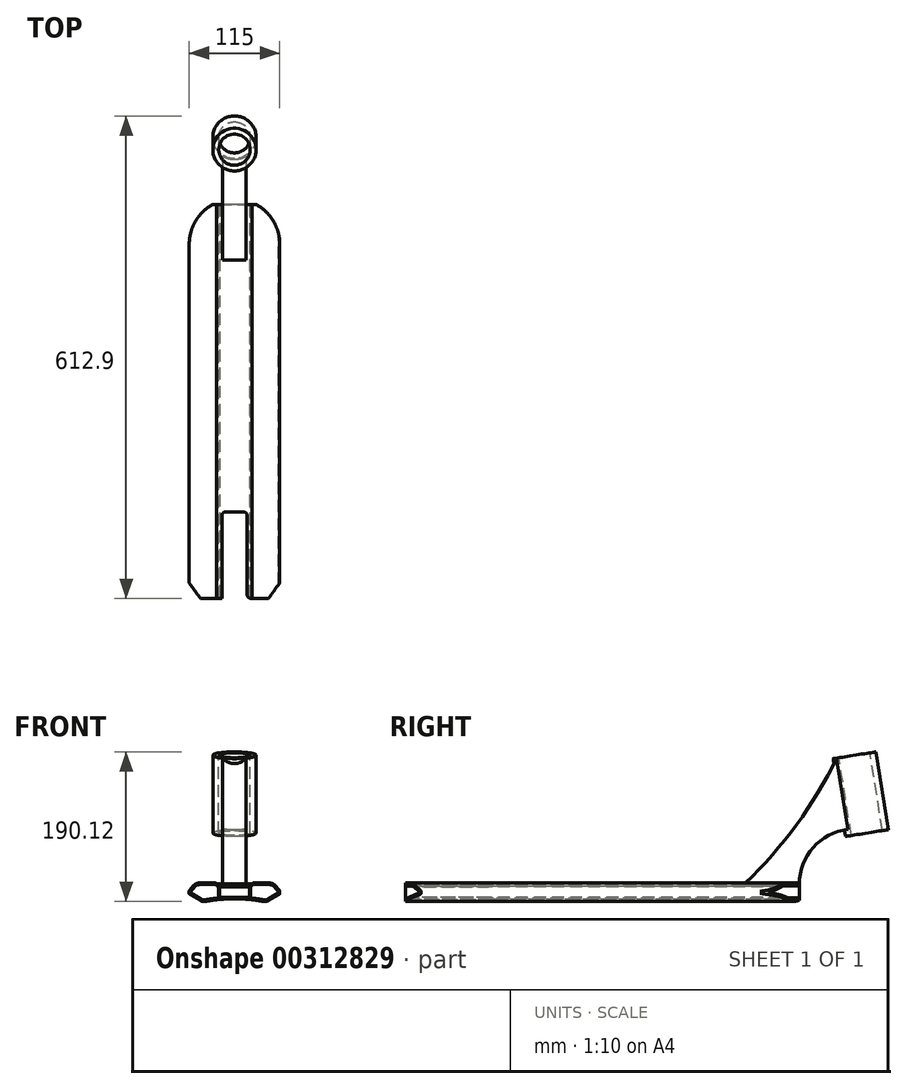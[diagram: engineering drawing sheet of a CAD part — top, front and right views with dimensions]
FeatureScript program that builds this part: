
annotation { "Feature Type Name" : "Feature", "Feature Type Description" : "" }
export const myFeature = defineFeature(function(context is Context, id is Id, definition is map)
    precondition{}
    {
        {
            var Q0;
            Q0=qCreatedBy(makeId("Front.planeOp"),FACE);
            var sketch = newSketch(context, id + "F0", { "sketchPlane" : qUnion([Q0])});
            skLineSegment(sketch, "E0", {"start": v(0, 0) * mm, "end": v(0, 20.54) * mm, "construction": true});
            skLineSegment(sketch, "E1", {"start": v(0, 0) * mm, "end": v(22.5, 0) * mm});
            skLineSegment(sketch, "E2", {"start": v(22.5, 0) * mm, "end": v(22.5, 1.3) * mm});
            skLineSegment(sketch, "E3", {"start": v(22.5, 1.3) * mm, "end": v(49.1, 1.3) * mm});
            skLineSegment(sketch, "E4", {"start": v(57.5, -8.7) * mm, "end": v(49.1, 1.3) * mm});
            skLineSegment(sketch, "E5", {"start": v(57.5, -8.7) * mm, "end": v(57.5, -12.7) * mm});
            skLineSegment(sketch, "E6", {"start": v(57.5, -12.7) * mm, "end": v(40.18, -22.7) * mm});
            skLineSegment(sketch, "E7.MirrorCS", {"start": v(0, 0) * mm, "end": v(-22.5, 0) * mm});
            skLineSegment(sketch, "E8.MirrorCS", {"start": v(-22.5, 0) * mm, "end": v(-22.5, 1.3) * mm});
            skLineSegment(sketch, "E9.MirrorCS", {"start": v(-22.5, 1.3) * mm, "end": v(-49.1, 1.3) * mm});
            skLineSegment(sketch, "E10.MirrorCS", {"start": v(-57.5, -8.7) * mm, "end": v(-49.1, 1.3) * mm});
            skLineSegment(sketch, "E11.MirrorCS", {"start": v(-57.5, -8.7) * mm, "end": v(-57.5, -12.7) * mm});
            skLineSegment(sketch, "E12.MirrorCS", {"start": v(-57.5, -12.7) * mm, "end": v(-40.18, -22.7) * mm});
            skArc(sketch, "E13", {"start": v(40.18, -22.7) * mm, "mid": v(0, -18.62) * mm, "end": v(-40.18, -22.7) * mm});
            skSolve(sketch);
        }
        {
            var Q0;
            Q0 = qSketchRegion(id + "F0", true);
            extrude(context, id + "F1", {"entities" : qUnion([Q0]), "endBound" : BoundingType.SYMMETRIC, "depth" : 500 * mm});
        }
        {
            var Q0;
            Q0=qCreatedBy(makeId("Front.planeOp"),FACE);
            var sketch = newSketch(context, id + "F2", { "sketchPlane" : qUnion([Q0])});
            skLineSegment(sketch, "E14.bottom", {"start": v(-19, -16.75) * mm, "end": v(19, -16.75) * mm});
            skLineSegment(sketch, "E14.top", {"start": v(-19, -3.75) * mm, "end": v(19, -3.75) * mm});
            skLineSegment(sketch, "E14.left", {"start": v(-19, -16.75) * mm, "end": v(-19, -3.75) * mm});
            skLineSegment(sketch, "E14.right", {"start": v(19, -16.75) * mm, "end": v(19, -3.75) * mm});
            skPoint(sketch, "E14.middle", {"position": v(0, -10.25) * mm});
            skSolve(sketch);
        }
        {
            var Q0;
            Q0 = qSketchRegion(id + "F2", true);
            extrude(context, id + "F3", {"entities" : qUnion([Q0]), "operationType" : NewBodyOperationType.REMOVE, "endBound" : BoundingType.SYMMETRIC, "oppositeDirection" : true, "depth" : 500 * mm});
        }
        {
            var Q0;
            Q0=makeQuery(id+"F1.opExtrude","SWEPT_EDGE",EDGE,{"disambiguationData":[OSD([sQuery(id+"F0.wireOp",EDGE,"E2"),sQuery(id+"F0.wireOp",EDGE,"E3")])]});
            var Q1;
            Q1=makeQuery(id+"F1.opExtrude","SWEPT_EDGE",EDGE,{"disambiguationData":[OSD([sQuery(id+"F0.wireOp",EDGE,"E8.MirrorCS"),sQuery(id+"F0.wireOp",EDGE,"E9.MirrorCS")])]});
            fillet(context, id + "F4", {"entities" : qUnion([Q0, Q1]), "radius" : 2 * mm, "tangentPropagation" : true, "allowEdgeOverflow" : false});
        }
        {
            var Q0;
            Q0=makeQuery(id+"F1.opExtrude","SWEPT_EDGE",EDGE,{"disambiguationData":[OSD([sQuery(id+"F0.wireOp",EDGE,"E9.MirrorCS"),sQuery(id+"F0.wireOp",EDGE,"E10.MirrorCS")])]});
            var Q1;
            Q1=makeQuery(id+"F1.opExtrude","SWEPT_EDGE",EDGE,{"disambiguationData":[OSD([sQuery(id+"F0.wireOp",EDGE,"E3"),sQuery(id+"F0.wireOp",EDGE,"E4")])]});
            var Q2;
            Q2=makeQuery(id+"F1.opExtrude","SWEPT_EDGE",EDGE,{"disambiguationData":[OSD([sQuery(id+"F0.wireOp",EDGE,"E6"),sQuery(id+"F0.wireOp",EDGE,"E13")])]});
            var Q3;
            Q3=makeQuery(id+"F1.opExtrude","SWEPT_EDGE",EDGE,{"disambiguationData":[OSD([sQuery(id+"F0.wireOp",EDGE,"E12.MirrorCS"),sQuery(id+"F0.wireOp",EDGE,"E13")])]});
            fillet(context, id + "F5", {"entities" : qUnion([Q0, Q1, Q2, Q3]), "radius" : 9 * mm, "tangentPropagation" : true, "allowEdgeOverflow" : false});
        }
        {
            var Q0;
            Q0=makeQuery(id+"F1.opExtrude","SWEPT_EDGE",EDGE,{"disambiguationData":[OSD([sQuery(id+"F0.wireOp",EDGE,"E10.MirrorCS"),sQuery(id+"F0.wireOp",EDGE,"E11.MirrorCS")])]});
            var Q1;
            Q1=makeQuery(id+"F1.opExtrude","SWEPT_EDGE",EDGE,{"disambiguationData":[OSD([sQuery(id+"F0.wireOp",EDGE,"E11.MirrorCS"),sQuery(id+"F0.wireOp",EDGE,"E12.MirrorCS")])]});
            var Q2;
            Q2=makeQuery(id+"F1.opExtrude","SWEPT_EDGE",EDGE,{"disambiguationData":[OSD([sQuery(id+"F0.wireOp",EDGE,"E4"),sQuery(id+"F0.wireOp",EDGE,"E5")])]});
            var Q3;
            Q3=makeQuery(id+"F1.opExtrude","SWEPT_EDGE",EDGE,{"disambiguationData":[OSD([sQuery(id+"F0.wireOp",EDGE,"E5"),sQuery(id+"F0.wireOp",EDGE,"E6")])]});
            fillet(context, id + "F6", {"entities" : qUnion([Q0, Q1, Q2, Q3]), "radius" : 2 * mm, "tangentPropagation" : true, "allowEdgeOverflow" : false});
        }
        {
            var Q0;
            Q0=makeQuery(id+"F1.opExtrude","CAP_FACE",FACE,{"disambiguationData":[OSD([sQuery(id+"F0.wireOp",EDGE,"E1"),sQuery(id+"F0.wireOp",EDGE,"E2"),sQuery(id+"F0.wireOp",EDGE,"E3"),sQuery(id+"F0.wireOp",EDGE,"E4"),sQuery(id+"F0.wireOp",EDGE,"E5"),sQuery(id+"F0.wireOp",EDGE,"E6"),sQuery(id+"F0.wireOp",EDGE,"E7.MirrorCS"),sQuery(id+"F0.wireOp",EDGE,"E8.MirrorCS"),sQuery(id+"F0.wireOp",EDGE,"E9.MirrorCS"),sQuery(id+"F0.wireOp",EDGE,"E10.MirrorCS"),sQuery(id+"F0.wireOp",EDGE,"E11.MirrorCS"),sQuery(id+"F0.wireOp",EDGE,"E12.MirrorCS"),sQuery(id+"F0.wireOp",EDGE,"E13")])],"isStart":false});
            var sketch = newSketch(context, id + "F7", { "sketchPlane" : qUnion([Q0])});
            skArc(sketch, "E15.0", {"start": v(-20.4, -17.65) * mm, "mid": v(-28.88, -18.7) * mm, "end": v(-37.3, -20.1) * mm});
            skArc(sketch, "E15.1", {"start": v(-42.1, -19.28) * mm, "mid": v(-39.78, -20.12) * mm, "end": v(-37.3, -20.1) * mm});
            skLineSegment(sketch, "E15.2", {"start": v(-24.37, -0.7) * mm, "end": v(-44.91, -0.7) * mm});
            skArc(sketch, "E15.3", {"start": v(-44.91, -0.7) * mm, "mid": v(-47.87, -1.36) * mm, "end": v(-50.27, -3.2) * mm});
            skLineSegment(sketch, "E15.4", {"start": v(-55.93, -9.94) * mm, "end": v(-50.27, -3.2) * mm});
            skLineSegment(sketch, "E15.5", {"start": v(-55.66, -11.45) * mm, "end": v(-42.1, -19.28) * mm});
            skPoint(sketch, "E16.visualSharp", {"position": v(-56.7, -10.85) * mm});
            skArc(sketch, "E16.filletArc", {"start": v(-55.93, -9.94) * mm, "mid": v(-56.15, -10.76) * mm, "end": v(-55.66, -11.45) * mm});
            skArc(sketch, "E17", {"start": v(-24.37, -0.7) * mm, "mid": v(-23.06, -1.19) * mm, "end": v(-22.4, -2.41) * mm});
            skLineSegment(sketch, "E18", {"start": v(-22.4, -2.41) * mm, "end": v(-20.4, -2.41) * mm});
            skLineSegment(sketch, "E19", {"start": v(-20.4, -2.41) * mm, "end": v(-20.4, -17.65) * mm});
            skLineSegment(sketch, "E20", {"start": v(0, 0) * mm, "end": v(0, 20.39) * mm, "construction": true});
            skPoint(sketch, "E20.endSnap0", {"position": v(0, 0) * mm});
            skLineSegment(sketch, "E21.MirrorCS", {"start": v(20.4, -2.41) * mm, "end": v(20.4, -17.65) * mm});
            skLineSegment(sketch, "E22.MirrorCS", {"start": v(22.4, -2.41) * mm, "end": v(20.4, -2.41) * mm});
            skArc(sketch, "E23.MirrorCS", {"start": v(24.37, -0.7) * mm, "mid": v(23.06, -1.19) * mm, "end": v(22.4, -2.41) * mm});
            skLineSegment(sketch, "E24.MirrorCS", {"start": v(24.37, -0.7) * mm, "end": v(44.91, -0.7) * mm});
            skArc(sketch, "E25.MirrorCS", {"start": v(44.91, -0.7) * mm, "mid": v(47.87, -1.36) * mm, "end": v(50.27, -3.2) * mm});
            skLineSegment(sketch, "E26.MirrorCS", {"start": v(55.93, -9.94) * mm, "end": v(50.27, -3.2) * mm});
            skLineSegment(sketch, "E27.MirrorCS", {"start": v(55.66, -11.45) * mm, "end": v(42.1, -19.28) * mm});
            skArc(sketch, "E28.MirrorCS", {"start": v(42.1, -19.28) * mm, "mid": v(39.78, -20.12) * mm, "end": v(37.3, -20.1) * mm});
            skArc(sketch, "E29.MirrorCS", {"start": v(20.4, -17.65) * mm, "mid": v(28.88, -18.7) * mm, "end": v(37.3, -20.1) * mm});
            skArc(sketch, "E30.MirrorCS", {"start": v(55.93, -9.94) * mm, "mid": v(56.15, -10.76) * mm, "end": v(55.66, -11.45) * mm});
            skSolve(sketch);
        }
        {
            var Q0;
            Q0 = qSketchRegion(id + "F7", true);
            extrude(context, id + "F8", {"entities" : qUnion([Q0]), "operationType" : NewBodyOperationType.REMOVE, "endBound" : BoundingType.THROUGH_ALL, "depth" : 25 * mm, "hasSecondDirection" : true, "secondDirectionBound" : SecondDirectionBoundingType.THROUGH_ALL, "secondDirectionOppositeDirection" : true, "secondDirectionDepth" : 25 * mm});
        }
        {
            var Q0;
            Q0=qCreatedBy(makeId("Top.planeOp"),FACE);
            var sketch = newSketch(context, id + "F9", { "sketchPlane" : qUnion([Q0])});
            skArc(sketch, "E31", {"start": v(57.5, 200) * mm, "mid": v(0, 257.5) * mm, "end": v(-57.5, 200) * mm});
            skLineSegment(sketch, "E32", {"start": v(-57.5, 200) * mm, "end": v(-57.5, 280) * mm});
            skLineSegment(sketch, "E33", {"start": v(-57.5, 280) * mm, "end": v(57.5, 280) * mm});
            skLineSegment(sketch, "E34", {"start": v(57.5, 280) * mm, "end": v(57.5, 200) * mm});
            skSolve(sketch);
        }
        {
            var Q0;
            Q0 = qSketchRegion(id + "F9", true);
            extrude(context, id + "F10", {"entities" : qUnion([Q0]), "operationType" : NewBodyOperationType.REMOVE, "endBound" : BoundingType.THROUGH_ALL, "oppositeDirection" : true, "depth" : 25 * mm, "hasSecondDirection" : true, "secondDirectionBound" : SecondDirectionBoundingType.THROUGH_ALL, "secondDirectionOppositeDirection" : false, "secondDirectionDepth" : 25 * mm});
        }
        {
            var Q0;
            Q0=qCreatedBy(makeId("Top.planeOp"),FACE);
            var sketch = newSketch(context, id + "F11", { "sketchPlane" : qUnion([Q0])});
            skLineSegment(sketch, "E35", {"start": v(-68, -216) * mm, "end": v(-43.3, -250) * mm});
            skLineSegment(sketch, "E36", {"start": v(-43.3, -250) * mm, "end": v(-16, -250) * mm});
            skLineSegment(sketch, "E37", {"start": v(-16, -250) * mm, "end": v(-16, -140) * mm});
            skLineSegment(sketch, "E38", {"start": v(-16, -140) * mm, "end": v(16, -140) * mm});
            skLineSegment(sketch, "E39", {"start": v(16, -140) * mm, "end": v(16, -250) * mm});
            skLineSegment(sketch, "E40", {"start": v(16, -250) * mm, "end": v(43.3, -250) * mm});
            skLineSegment(sketch, "E41", {"start": v(43.3, -250) * mm, "end": v(68, -216) * mm});
            skLineSegment(sketch, "E42", {"start": v(68, -216) * mm, "end": v(68, -346) * mm});
            skLineSegment(sketch, "E43", {"start": v(68, -346) * mm, "end": v(-68, -346) * mm});
            skLineSegment(sketch, "E44", {"start": v(-68, -346) * mm, "end": v(-68, -216) * mm});
            skSolve(sketch);
        }
        {
            var Q0;
            Q0 = qSketchRegion(id + "F11", true);
            extrude(context, id + "F12", {"entities" : qUnion([Q0]), "operationType" : NewBodyOperationType.REMOVE, "endBound" : BoundingType.THROUGH_ALL, "depth" : 25 * mm, "hasSecondDirection" : true, "secondDirectionBound" : SecondDirectionBoundingType.THROUGH_ALL, "secondDirectionOppositeDirection" : true, "secondDirectionDepth" : 25 * mm});
        }
        {
            var Q0;
            {var subQ2=sQuery(id+"F11.wireOp",EDGE,"E39");Q0=makeQuery(id+"F12.boolean.opBoolean","COPY",EDGE,{"disambiguationData":[TD([makeQuery(id+"F3.boolean.opBoolean","COPY",FACE,{"derivedFrom":makeQuery(id+"F3.opExtrude","SWEPT_FACE",FACE,{"disambiguationData":[OSD([sQuery(id+"F2.wireOp",EDGE,"E14.top")])]})})])],"derivedFrom":makeQuery(id+"F12.opExtrude","SWEPT_EDGE",EDGE,{"disambiguationData":[OSD([subQ2,sQuery(id+"F11.wireOp",EDGE,"E40")])]})});}
            var Q1;
            {var subQ2=sQuery(id+"F11.wireOp",EDGE,"E37");Q1=makeQuery(id+"F12.boolean.opBoolean","COPY",EDGE,{"disambiguationData":[TD([makeQuery(id+"F3.boolean.opBoolean","COPY",FACE,{"derivedFrom":makeQuery(id+"F3.opExtrude","SWEPT_FACE",FACE,{"disambiguationData":[OSD([sQuery(id+"F2.wireOp",EDGE,"E14.top")])]})})])],"derivedFrom":makeQuery(id+"F12.opExtrude","SWEPT_EDGE",EDGE,{"disambiguationData":[OSD([sQuery(id+"F11.wireOp",EDGE,"E36"),subQ2])]})});}
            var Q2;
            {var subQ0=sQuery(id+"F11.wireOp",EDGE,"E37");var subQ1=sQuery(id+"F11.wireOp",EDGE,"E38");Q2=makeQuery(id+"F12.boolean.opBoolean","COPY",EDGE,{"disambiguationData":[TD([makeQuery(id+"F3.boolean.opBoolean","COPY",FACE,{"derivedFrom":makeQuery(id+"F3.opExtrude","SWEPT_FACE",FACE,{"disambiguationData":[OSD([sQuery(id+"F2.wireOp",EDGE,"E14.top")])]})})])],"derivedFrom":makeQuery(id+"F12.opExtrude","SWEPT_EDGE",EDGE,{"disambiguationData":[OSD([subQ0,subQ1])]})});}
            var Q3;
            {var subQ0=sQuery(id+"F11.wireOp",EDGE,"E38");var subQ1=sQuery(id+"F11.wireOp",EDGE,"E37");Q3=makeQuery(id+"F12.boolean.opBoolean","COPY",EDGE,{"disambiguationData":[TD([makeQuery(id+"F1.opExtrude","SWEPT_FACE",FACE,{"disambiguationData":[OSD([sQuery(id+"F0.wireOp",EDGE,"E13")])]})])],"derivedFrom":makeQuery(id+"F12.opExtrude","SWEPT_EDGE",EDGE,{"disambiguationData":[OSD([subQ1,subQ0])]})});}
            var Q4;
            {var subQ0=sQuery(id+"F11.wireOp",EDGE,"E39");var subQ1=sQuery(id+"F11.wireOp",EDGE,"E38");Q4=makeQuery(id+"F12.boolean.opBoolean","COPY",EDGE,{"disambiguationData":[TD([makeQuery(id+"F3.boolean.opBoolean","COPY",FACE,{"derivedFrom":makeQuery(id+"F3.opExtrude","SWEPT_FACE",FACE,{"disambiguationData":[OSD([sQuery(id+"F2.wireOp",EDGE,"E14.top")])]})})])],"derivedFrom":makeQuery(id+"F12.opExtrude","SWEPT_EDGE",EDGE,{"disambiguationData":[OSD([subQ1,subQ0])]})});}
            var Q5;
            {var subQ0=sQuery(id+"F11.wireOp",EDGE,"E38");var subQ1=sQuery(id+"F11.wireOp",EDGE,"E39");Q5=makeQuery(id+"F12.boolean.opBoolean","COPY",EDGE,{"disambiguationData":[TD([makeQuery(id+"F1.opExtrude","SWEPT_FACE",FACE,{"disambiguationData":[OSD([sQuery(id+"F0.wireOp",EDGE,"E13")])]})])],"derivedFrom":makeQuery(id+"F12.opExtrude","SWEPT_EDGE",EDGE,{"disambiguationData":[OSD([subQ0,subQ1])]})});}
            fillet(context, id + "F13", {"entities" : qUnion([Q0, Q1, Q2, Q3, Q4, Q5]), "radius" : 5 * mm, "tangentPropagation" : true, "allowEdgeOverflow" : false});
        }
        {
            var Q0;
            Q0=qCreatedBy(makeId("Right.planeOp"),FACE);
            var sketch = newSketch(context, id + "F14", { "sketchPlane" : qUnion([Q0])});
            skLineSegment(sketch, "E45", {"start": v(180, 0) * mm, "end": v(250, 0) * mm});
            skArc(sketch, "E46", {"start": v(180, 0) * mm, "mid": v(245.97, 74.66) * mm, "end": v(297.38, 160) * mm});
            skLineSegment(sketch, "E47", {"start": v(297.38, 160) * mm, "end": v(342.82, 167.2) * mm});
            skLineSegment(sketch, "E48", {"start": v(342.82, 167.2) * mm, "end": v(358.46, 68.43) * mm});
            skLineSegment(sketch, "E49", {"start": v(358.46, 68.43) * mm, "end": v(313.03, 61.23) * mm});
            skLineSegment(sketch, "E50", {"start": v(313.03, 61.23) * mm, "end": v(311.71, 69.5) * mm});
            skArc(sketch, "E51", {"start": v(311.71, 69.5) * mm, "mid": v(267.66, 46.48) * mm, "end": v(250, 0) * mm});
            skSolve(sketch);
        }
        {
            var Q0;
            Q0 = qSketchRegion(id + "F14", true);
            extrude(context, id + "F15", {"entities" : qUnion([Q0]), "operationType" : NewBodyOperationType.ADD, "endBound" : BoundingType.SYMMETRIC, "depth" : 30 * mm});
        }
        {
            var Q0;
            Q0=makeQuery(id+"F15.opExtrude","SWEPT_FACE",FACE,{"disambiguationData":[OSD([sQuery(id+"F14.wireOp",EDGE,"E47")])]});
            var sketch = newSketch(context, id + "F16", { "sketchPlane" : qUnion([Q0])});
            skCircle(sketch, "E52", {"center": v(0, 341.75) * mm, "radius": 27.5 * mm});
            skSolve(sketch);
        }
        {
            var Q0;
            Q0 = qSketchRegion(id + "F16", true);
            var Q1;
            Q1=makeQuery(id+"F15.opExtrude","SWEPT_FACE",FACE,{"disambiguationData":[OSD([sQuery(id+"F14.wireOp",EDGE,"E49")])]});
            extrude(context, id + "F17", {"entities" : qUnion([Q0]), "operationType" : NewBodyOperationType.ADD, "endBound" : BoundingType.UP_TO_SURFACE, "oppositeDirection" : true, "endBoundEntityFace" : qUnion([Q1]), "depth" : 25 * mm});
        }
        {
            var Q0;
            Q0=makeQuery(id+"F17.boolean.opBoolean","MERGE",FACE,{"derivedFrom":[makeQuery(id+"F15.opExtrude","SWEPT_FACE",FACE,{"disambiguationData":[OSD([sQuery(id+"F14.wireOp",EDGE,"E47")])]}),makeQuery(id+"F17.opExtrude","CAP_FACE",FACE,{"disambiguationData":[OSD([sQuery(id+"F16.wireOp",EDGE,"E52")])],"isStart":true})]});
            var sketch = newSketch(context, id + "F18", { "sketchPlane" : qUnion([Q0])});
            skPoint(sketch, "E53", {"position": v(0, 341.75) * mm});
            skSolve(sketch);
        }
        {
            var Q0;
            Q0=sQuery(id+"F18.wireOp",VERTEX,"E53");
            var Q1;
            Q1=makeQuery(id+"F1.opExtrude","SWEPT_BODY",BODY,{"disambiguationData":[OSD([sQuery(id+"F0.wireOp",EDGE,"E1"),sQuery(id+"F0.wireOp",EDGE,"E2"),sQuery(id+"F0.wireOp",EDGE,"E3"),sQuery(id+"F0.wireOp",EDGE,"E4"),sQuery(id+"F0.wireOp",EDGE,"E5"),sQuery(id+"F0.wireOp",EDGE,"E6"),sQuery(id+"F0.wireOp",EDGE,"E7.MirrorCS"),sQuery(id+"F0.wireOp",EDGE,"E8.MirrorCS"),sQuery(id+"F0.wireOp",EDGE,"E9.MirrorCS"),sQuery(id+"F0.wireOp",EDGE,"E10.MirrorCS"),sQuery(id+"F0.wireOp",EDGE,"E11.MirrorCS"),sQuery(id+"F0.wireOp",EDGE,"E12.MirrorCS"),sQuery(id+"F0.wireOp",EDGE,"E13")])]});
            hole(context, id + "F19", {"style" : HoleStyle.SIMPLE, "endStyle" : HoleEndStyle.THROUGH, "holeDiameter" : 40 * mm, "isTappedThrough" : true, "tappedDepth" : 12 * mm, "tapClearance" : 3, "locations" : qUnion([Q0]), "scope" : qUnion([Q1])});
        }
    });
